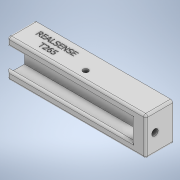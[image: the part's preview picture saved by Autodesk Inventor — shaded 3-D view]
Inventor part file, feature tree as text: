
AUTODESK INVENTOR PART (.ipt)
format: ipt  version: 2021.4 (Build 254397000, 397)  size: 442,880 bytes
history: native  units: mm
features: sketch x7, extrude x4, hole x3, other x1, fillet x1
ambient origin geometry x8: Origin, YZ Plane, XZ Plane, XY Plane, X Axis, Y Axis, Z Axis, Center Point
bodies: Body1 (feature_tree)
feature tree (16):
  other  "ソリッド1"
  extrude  "押し出し1"  Depth=128.0mm
  extrude  "押し出し2"  Depth=35.0mm
  hole  "穴2"  [1 undecoded]
  hole  "穴3"  [1 undecoded]
  hole  "穴4"  [1 undecoded]
  extrude  "押し出し7"  Depth=4.5mm
  fillet  "フィレット3"  Radius=2.0mm
  extrude  "押し出し8"  Depth=118.0mm TaperAngle=0.0deg
  sketch  "スケッチ1"
  sketch  "スケッチ3"
  sketch  "スケッチ6"
  sketch  "スケッチ7"
  sketch  "スケッチ8"
  sketch  "スケッチ12"
  sketch  "スケッチ13"
note: 3 required parameter values undecoded (feature->parameter linkage not recoverable at this tier; creation-order binding heuristic only, values carry confidence <= 0.55)
